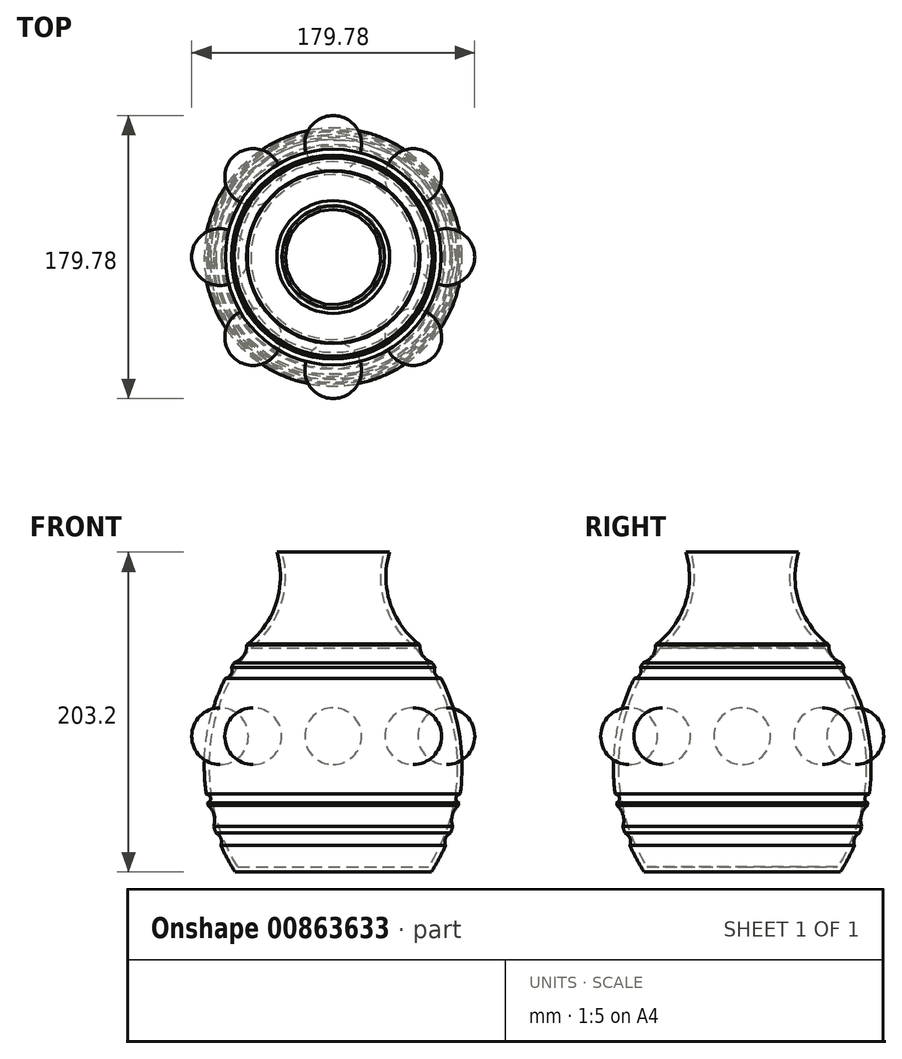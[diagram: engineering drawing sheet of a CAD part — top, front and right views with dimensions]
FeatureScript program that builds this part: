
annotation { "Feature Type Name" : "Feature", "Feature Type Description" : "" }
export const myFeature = defineFeature(function(context is Context, id is Id, definition is map)
    precondition{}
    {
        {
            var Q0;
            Q0=qCreatedBy(makeId("Front.planeOp"),FACE);
            var sketch = newSketch(context, id + "F0", { "sketchPlane" : qUnion([Q0])});
            skLineSegment(sketch, "E0", {"start": v(0, 0) * mm, "end": v(0, 203.2) * mm});
            skLineSegment(sketch, "E1", {"start": v(0, 0) * mm, "end": v(62.29, 0) * mm});
            skLineSegment(sketch, "E2", {"start": v(0, 203.2) * mm, "end": v(35.81, 203.2) * mm});
            skArc(sketch, "E3", {"start": v(35.81, 203.2) * mm, "mid": v(36.06, 171.05) * mm, "end": v(54.52, 144.73) * mm});
            skArc(sketch, "E4", {"start": v(62.29, 0) * mm, "mid": v(81.7, 73.62) * mm, "end": v(54.52, 144.73) * mm});
            skSolve(sketch);
        }
        {
            var Q0;
            Q0=makeQuery(id+"F0.imprint","IMPRINT",FACE,{"disambiguationData":[TD([[makeQuery(id+"F0.imprint","IMPRINT",EDGE,{"derivedFrom":sQuery(id+"F0.wireOp",EDGE,"E0")}),-1.0]])]});
            var Q1;
            Q1=sQuery(id+"F0.wireOp",EDGE,"E0");
            revolve(context, id + "F1", {"surfaceOperationType" : NewSurfaceOperationType.NEW, "entities" : qUnion([Q0]), "axis" : qUnion([Q1]), "revolveType" : RevolveType.FULL});
        }
        {
            var Q0;
            Q0=qCreatedBy(makeId("Front.planeOp"),FACE);
            var sketch = newSketch(context, id + "F2", { "sketchPlane" : qUnion([Q0])});
            skArc(sketch, "E5", {"start": v(120.13, 147.45) * mm, "mid": v(102.1, 129.42) * mm, "end": v(120.13, 111.4) * mm});
            skLineSegment(sketch, "E6", {"start": v(120.13, 111.4) * mm, "end": v(120.13, 147.45) * mm});
            skSolve(sketch);
        }
        {
            var Q0;
            Q0=makeQuery(id+"F2.imprint","IMPRINT",FACE,{"disambiguationData":[TD([[makeQuery(id+"F2.imprint","IMPRINT",EDGE,{"derivedFrom":sQuery(id+"F2.wireOp",EDGE,"E5")}),1.0]])]});
            var Q1;
            Q1=sQuery(id+"F2.wireOp",EDGE,"E6");
            revolve(context, id + "F3", {"surfaceOperationType" : NewSurfaceOperationType.NEW, "entities" : qUnion([Q0]), "axis" : qUnion([Q1]), "revolveType" : RevolveType.FULL});
        }
        {
            var Q0;
            Q0=makeQuery(id+"F3.opRevolve","SWEPT_BODY",BODY,{"disambiguationData":[OSD([sQuery(id+"F2.wireOp",EDGE,"E5"),sQuery(id+"F2.wireOp",EDGE,"E6")])]});
            transform(context, id + "F4", {"entities" : qUnion([Q0]), "transformType" : TransformType.TRANSLATION_3D, "dx" : -48.26 * mm, "dy" : 0 * mm, "dz" : -43.18 * mm, "makeCopy" : false});
        }
        {
            var Q0;
            Q0=makeQuery(id+"F3.opRevolve","SWEPT_BODY",BODY,{"disambiguationData":[OSD([sQuery(id+"F2.wireOp",EDGE,"E5"),sQuery(id+"F2.wireOp",EDGE,"E6")])]});
            var Q1;
            Q1=makeQuery(id+"F1.opRevolve","SWEPT_EDGE",EDGE,{"disambiguationData":[OSD([sQuery(id+"F0.wireOp",EDGE,"E3"),sQuery(id+"F0.wireOp",EDGE,"E4")])]});
            circularPattern(context, id + "F5", {"entities" : qUnion([Q0]), "axis" : qUnion([Q1]), "angle" : 360 * degree, "instanceCount" : 8, "equalSpace" : true});
        }
        {
            var Q0;
            Q0=makeQuery(id+"F1.opRevolve","SWEPT_FACE",FACE,{"disambiguationData":[OSD([sQuery(id+"F0.wireOp",EDGE,"E2")])]});
            shell(context, id + "F6", {"entities" : qUnion([Q0]), "thickness" : 3.17 * mm});
        }
        {
            var Q0;
            Q0=qCreatedBy(makeId("Front.planeOp"),FACE);
            var sketch = newSketch(context, id + "F7", { "sketchPlane" : qUnion([Q0])});
            skCircle(sketch, "E7", {"center": v(66.3, 143.75) * mm, "radius": 11.34 * mm});
            skSolve(sketch);
        }
        {
            var Q0;
            Q0=makeQuery(id+"F7.imprint","IMPRINT",FACE,{"disambiguationData":[TD([[makeQuery(id+"F7.imprint","IMPRINT",EDGE,{"derivedFrom":sQuery(id+"F7.wireOp",EDGE,"E7")}),1.0]])]});
            var Q1;
            Q1=makeQuery(id+"F6.opShell","OFFSET_EDGE",EDGE,{"disambiguationData":[OSD([sQuery(id+"F0.wireOp",EDGE,"E2"),sQuery(id+"F0.wireOp",EDGE,"E3")])]});
            revolve(context, id + "F8", {"operationType" : NewBodyOperationType.REMOVE, "surfaceOperationType" : NewSurfaceOperationType.NEW, "entities" : qUnion([Q0]), "axis" : qUnion([Q1]), "revolveType" : RevolveType.FULL, "oppositeDirection" : true});
        }
        {
            var Q0;
            Q0=qCreatedBy(makeId("Front.planeOp"),FACE);
            var sketch = newSketch(context, id + "F9", { "sketchPlane" : qUnion([Q0])});
            skCircle(sketch, "E8", {"center": v(89.9, 20.02) * mm, "radius": 13.77 * mm});
            skSolve(sketch);
        }
        {
            var Q0;
            Q0=makeQuery(id+"F9.imprint","IMPRINT",FACE,{"disambiguationData":[TD([[makeQuery(id+"F9.imprint","IMPRINT",EDGE,{"derivedFrom":sQuery(id+"F9.wireOp",EDGE,"E8")}),1.0]])]});
            var Q1;
            Q1=makeQuery(id+"F6.opShell","OFFSET_EDGE",EDGE,{"disambiguationData":[OSD([sQuery(id+"F0.wireOp",EDGE,"E1"),sQuery(id+"F0.wireOp",EDGE,"E4")])]});
            revolve(context, id + "F10", {"operationType" : NewBodyOperationType.REMOVE, "surfaceOperationType" : NewSurfaceOperationType.NEW, "entities" : qUnion([Q0]), "axis" : qUnion([Q1]), "revolveType" : RevolveType.FULL, "oppositeDirection" : true});
        }
        {
            var Q0;
            Q0=qCreatedBy(makeId("Front.planeOp"),FACE);
            var sketch = newSketch(context, id + "F11", { "sketchPlane" : qUnion([Q0])});
            skArc(sketch, "E9", {"start": v(85.61, 162.37) * mm, "mid": v(69.96, 146.72) * mm, "end": v(85.61, 131.06) * mm});
            skLineSegment(sketch, "E10", {"start": v(85.61, 131.06) * mm, "end": v(85.61, 162.37) * mm});
            skSolve(sketch);
        }
        {
            var Q0;
            Q0=makeQuery(id+"F11.imprint","IMPRINT",FACE,{"disambiguationData":[TD([[makeQuery(id+"F11.imprint","IMPRINT",EDGE,{"derivedFrom":sQuery(id+"F11.wireOp",EDGE,"E9")}),1.0]])]});
            var Q1;
            Q1=sQuery(id+"F11.wireOp",EDGE,"E10");
            revolve(context, id + "F12", {"surfaceOperationType" : NewSurfaceOperationType.NEW, "entities" : qUnion([Q0]), "axis" : qUnion([Q1]), "revolveType" : RevolveType.FULL});
        }
        {
            var Q0;
            Q0=makeQuery(id+"F12.opRevolve","SWEPT_BODY",BODY,{"disambiguationData":[OSD([sQuery(id+"F11.wireOp",EDGE,"E9"),sQuery(id+"F11.wireOp",EDGE,"E10")])]});
            transform(context, id + "F13", {"entities" : qUnion([Q0]), "transformType" : TransformType.TRANSLATION_3D, "dx" : -50.55 * mm, "dy" : 0 * mm, "dz" : 23.1 * mm, "makeCopy" : false});
        }
        {
            var Q0;
            Q0=makeQuery(id+"F12.opRevolve","SWEPT_BODY",BODY,{"disambiguationData":[OSD([sQuery(id+"F11.wireOp",EDGE,"E9"),sQuery(id+"F11.wireOp",EDGE,"E10")])]});
            var Q1;
            Q1=makeQuery(id+"F6.opShell","OFFSET_EDGE",EDGE,{"disambiguationData":[OSD([sQuery(id+"F0.wireOp",EDGE,"E2"),sQuery(id+"F0.wireOp",EDGE,"E3")])]});
            circularPattern(context, id + "F14", {"entities" : qUnion([Q0]), "axis" : qUnion([Q1]), "angle" : 360 * degree, "instanceCount" : 6, "equalSpace" : true});
        }
        {
            var Q0;
            Q0=makeQuery(id+"F14.opPattern","COPY",BODY,{"derivedFrom":makeQuery(id+"F12.opRevolve","SWEPT_BODY",BODY,{"disambiguationData":[OSD([sQuery(id+"F11.wireOp",EDGE,"E9"),sQuery(id+"F11.wireOp",EDGE,"E10")])]}),"instanceName":"3"});
            var Q1;
            Q1=makeQuery(id+"F14.opPattern","COPY",BODY,{"derivedFrom":makeQuery(id+"F12.opRevolve","SWEPT_BODY",BODY,{"disambiguationData":[OSD([sQuery(id+"F11.wireOp",EDGE,"E9"),sQuery(id+"F11.wireOp",EDGE,"E10")])]}),"instanceName":"4"});
            var Q2;
            Q2=makeQuery(id+"F14.opPattern","COPY",BODY,{"derivedFrom":makeQuery(id+"F12.opRevolve","SWEPT_BODY",BODY,{"disambiguationData":[OSD([sQuery(id+"F11.wireOp",EDGE,"E9"),sQuery(id+"F11.wireOp",EDGE,"E10")])]}),"instanceName":"5"});
            var Q3;
            Q3=makeQuery(id+"F14.opPattern","COPY",BODY,{"derivedFrom":makeQuery(id+"F12.opRevolve","SWEPT_BODY",BODY,{"disambiguationData":[OSD([sQuery(id+"F11.wireOp",EDGE,"E9"),sQuery(id+"F11.wireOp",EDGE,"E10")])]}),"instanceName":"1"});
            var Q4;
            Q4=makeQuery(id+"F14.opPattern","COPY",BODY,{"derivedFrom":makeQuery(id+"F12.opRevolve","SWEPT_BODY",BODY,{"disambiguationData":[OSD([sQuery(id+"F11.wireOp",EDGE,"E9"),sQuery(id+"F11.wireOp",EDGE,"E10")])]}),"instanceName":"2"});
            var Q5;
            Q5=makeQuery(id+"F12.opRevolve","SWEPT_BODY",BODY,{"disambiguationData":[OSD([sQuery(id+"F11.wireOp",EDGE,"E9"),sQuery(id+"F11.wireOp",EDGE,"E10")])]});
            var Q6;
            Q6=makeQuery(id+"F5.opPattern","COPY",BODY,{"derivedFrom":makeQuery(id+"F3.opRevolve","SWEPT_BODY",BODY,{"disambiguationData":[OSD([sQuery(id+"F2.wireOp",EDGE,"E5"),sQuery(id+"F2.wireOp",EDGE,"E6")])]}),"instanceName":"4"});
            booleanBodies(context, id + "F15", {"operationType" : BooleanOperationType.SUBTRACTION, "tools" : qUnion([Q0, Q1, Q2, Q3, Q4, Q5]), "targets" : qUnion([Q6])});
        }
        {
            var Q0;
            Q0=qCreatedBy(makeId("Front.planeOp"),FACE);
            var sketch = newSketch(context, id + "F16", { "sketchPlane" : qUnion([Q0])});
            skCircle(sketch, "E11", {"center": v(87.64, 32.88) * mm, "radius": 12.4 * mm});
            skSolve(sketch);
        }
        {
            var Q0;
            Q0=makeQuery(id+"F16.imprint","IMPRINT",FACE,{"disambiguationData":[TD([[makeQuery(id+"F16.imprint","IMPRINT",EDGE,{"derivedFrom":sQuery(id+"F16.wireOp",EDGE,"E11")}),1.0]])]});
            var Q1;
            Q1=makeQuery(id+"F6.opShell","OFFSET_EDGE",EDGE,{"disambiguationData":[OSD([sQuery(id+"F0.wireOp",EDGE,"E1"),sQuery(id+"F0.wireOp",EDGE,"E4")])]});
            revolve(context, id + "F17", {"operationType" : NewBodyOperationType.REMOVE, "surfaceOperationType" : NewSurfaceOperationType.NEW, "entities" : qUnion([Q0]), "axis" : qUnion([Q1]), "revolveType" : RevolveType.FULL, "oppositeDirection" : true});
        }
        {
            var Q0;
            Q0=qCreatedBy(makeId("Front.planeOp"),FACE);
            var sketch = newSketch(context, id + "F18", { "sketchPlane" : qUnion([Q0])});
            skCircle(sketch, "E12", {"center": v(77.01, 19.14) * mm, "radius": 6.14 * mm});
            skSolve(sketch);
        }
        {
            var Q0;
            Q0=makeQuery(id+"F18.imprint","IMPRINT",FACE,{"disambiguationData":[TD([[makeQuery(id+"F18.imprint","IMPRINT",EDGE,{"derivedFrom":sQuery(id+"F18.wireOp",EDGE,"E12")}),1.0]])]});
            var Q1;
            Q1=makeQuery(id+"F6.opShell","OFFSET_EDGE",EDGE,{"disambiguationData":[OSD([sQuery(id+"F0.wireOp",EDGE,"E1"),sQuery(id+"F0.wireOp",EDGE,"E4")])]});
            revolve(context, id + "F19", {"operationType" : NewBodyOperationType.REMOVE, "surfaceOperationType" : NewSurfaceOperationType.NEW, "entities" : qUnion([Q0]), "axis" : qUnion([Q1]), "revolveType" : RevolveType.FULL, "oppositeDirection" : true});
        }
        {
            var Q0;
            Q0=qCreatedBy(makeId("Front.planeOp"),FACE);
            var sketch = newSketch(context, id + "F20", { "sketchPlane" : qUnion([Q0])});
            skCircle(sketch, "E13", {"center": v(80.76, 46.63) * mm, "radius": 2.83 * mm});
            skSolve(sketch);
        }
        {
            var Q0;
            Q0=makeQuery(id+"F20.imprint","IMPRINT",FACE,{"disambiguationData":[TD([[makeQuery(id+"F20.imprint","IMPRINT",EDGE,{"derivedFrom":sQuery(id+"F20.wireOp",EDGE,"E13")}),1.0]])]});
            var Q1;
            Q1=makeQuery(id+"F6.opShell","OFFSET_EDGE",EDGE,{"disambiguationData":[OSD([sQuery(id+"F0.wireOp",EDGE,"E1"),sQuery(id+"F0.wireOp",EDGE,"E4")])]});
            revolve(context, id + "F21", {"operationType" : NewBodyOperationType.REMOVE, "surfaceOperationType" : NewSurfaceOperationType.NEW, "entities" : qUnion([Q0]), "axis" : qUnion([Q1]), "revolveType" : RevolveType.FULL, "oppositeDirection" : true});
        }
        {
            var Q0;
            Q0=qCreatedBy(makeId("Front.planeOp"),FACE);
            var sketch = newSketch(context, id + "F22", { "sketchPlane" : qUnion([Q0])});
            skCircle(sketch, "E14", {"center": v(69.08, 127.87) * mm, "radius": 4.83 * mm});
            skSolve(sketch);
        }
        {
            var Q0;
            Q0=makeQuery(id+"F22.imprint","IMPRINT",FACE,{"disambiguationData":[TD([[makeQuery(id+"F22.imprint","IMPRINT",EDGE,{"derivedFrom":sQuery(id+"F22.wireOp",EDGE,"E14")}),1.0]])]});
            var Q1;
            Q1=makeQuery(id+"F8.boolean.opBoolean","INTERSECT",EDGE,{"disambiguationData":[OD(0.0)],"derivedFrom":[makeQuery(id+"F1.opRevolve","SWEPT_FACE",FACE,{"disambiguationData":[OSD([sQuery(id+"F0.wireOp",EDGE,"E4")])]}),makeQuery(id+"F8.opRevolve","SWEPT_FACE",FACE,{"disambiguationData":[OSD([sQuery(id+"F7.wireOp",EDGE,"E7")])]})]});
            revolve(context, id + "F23", {"operationType" : NewBodyOperationType.REMOVE, "surfaceOperationType" : NewSurfaceOperationType.NEW, "entities" : qUnion([Q0]), "axis" : qUnion([Q1]), "revolveType" : RevolveType.FULL, "oppositeDirection" : true});
        }
    });
